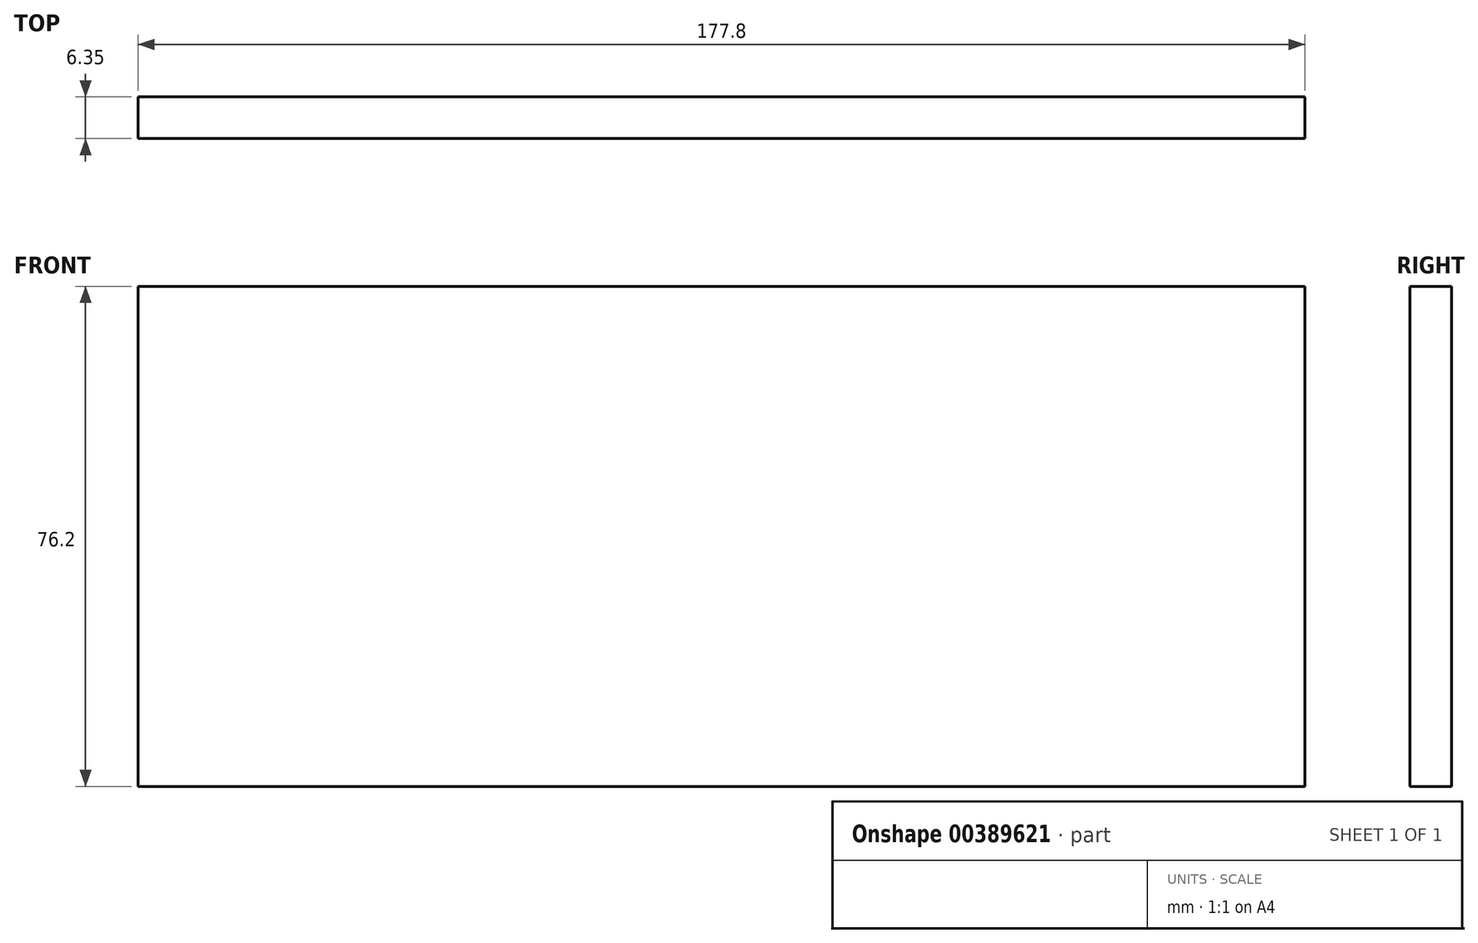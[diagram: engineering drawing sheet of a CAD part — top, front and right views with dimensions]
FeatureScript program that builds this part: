
annotation { "Feature Type Name" : "Feature", "Feature Type Description" : "" }
export const myFeature = defineFeature(function(context is Context, id is Id, definition is map)
    precondition{}
    {
        {
            var Q0;
            Q0=qCreatedBy(makeId("Front.planeOp"),FACE);
            var sketch = newSketch(context, id + "F0", { "sketchPlane" : qUnion([Q0])});
            skLineSegment(sketch, "E0.bottom", {"start": v(-72.45, 28.64) * mm, "end": v(105.35, 28.64) * mm});
            skLineSegment(sketch, "E0.top", {"start": v(-72.45, -47.56) * mm, "end": v(105.35, -47.56) * mm});
            skLineSegment(sketch, "E0.left", {"start": v(-72.45, 28.64) * mm, "end": v(-72.45, -47.56) * mm});
            skLineSegment(sketch, "E0.right", {"start": v(105.35, 28.64) * mm, "end": v(105.35, -47.56) * mm});
            skSolve(sketch);
        }
        {
            var Q0;
            Q0=makeQuery(id+"F0.imprint","IMPRINT",FACE,{"disambiguationData":[TD([[makeQuery(id+"F0.imprint","IMPRINT",EDGE,{"derivedFrom":sQuery(id+"F0.wireOp",EDGE,"E0.bottom")}),-1.0]])]});
            extrude(context, id + "F1", {"entities" : qUnion([Q0]), "depth" : 6.35 * mm});
        }
    });
